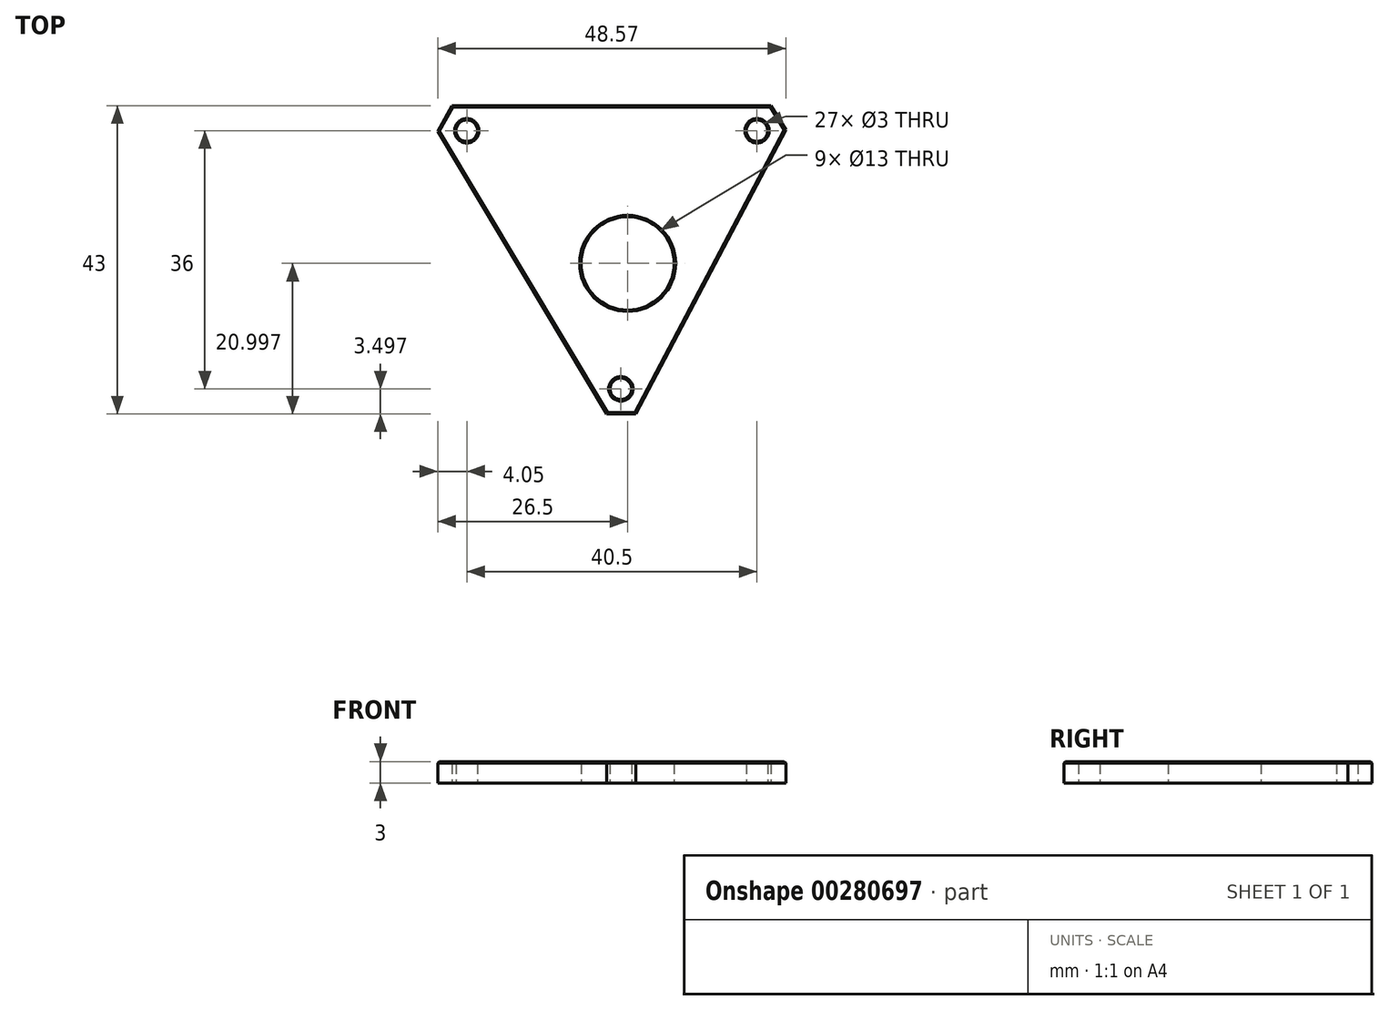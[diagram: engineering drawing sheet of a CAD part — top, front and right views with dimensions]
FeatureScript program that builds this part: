
annotation { "Feature Type Name" : "Feature", "Feature Type Description" : "" }
export const myFeature = defineFeature(function(context is Context, id is Id, definition is map)
    precondition{}
    {
        {
            var Q0;
            Q0=qCreatedBy(makeId("Top.planeOp"),FACE);
            var sketch = newSketch(context, id + "F0", { "sketchPlane" : qUnion([Q0])});
            skCircle(sketch, "E0", {"center": v(-29.37, -2.35) * mm, "radius": 1.5 * mm});
            skLineSegment(sketch, "E1", {"start": v(-29.37, -2.35) * mm, "end": v(-27.87, -2.35) * mm, "construction": true});
            skCircle(sketch, "E2", {"center": v(11.13, -2.35) * mm, "radius": 1.5 * mm});
            skCircle(sketch, "E3", {"center": v(-7.87, -38.35) * mm, "radius": 1.5 * mm});
            skLineSegment(sketch, "E4", {"start": v(-29.37, -2.35) * mm, "end": v(11.13, -2.35) * mm, "construction": true});
            skLineSegment(sketch, "E5", {"start": v(-7.87, -38.35) * mm, "end": v(-7.87, -2.35) * mm, "construction": true});
            skLineSegment(sketch, "E6.bottom", {"start": v(-32.87, 1.15) * mm, "end": v(14.63, 1.15) * mm, "construction": true});
            skLineSegment(sketch, "E6.top", {"start": v(-32.87, -41.85) * mm, "end": v(14.63, -41.85) * mm, "construction": true});
            skLineSegment(sketch, "E6.left", {"start": v(-32.87, 1.15) * mm, "end": v(-32.87, -41.85) * mm, "construction": true});
            skLineSegment(sketch, "E6.right", {"start": v(14.63, 1.15) * mm, "end": v(14.63, -41.85) * mm, "construction": true});
            skLineSegment(sketch, "E7", {"start": v(-29.37, -2.35) * mm, "end": v(-32.87, -2.35) * mm, "construction": true});
            skLineSegment(sketch, "E8", {"start": v(-29.37, -2.35) * mm, "end": v(-29.37, 1.15) * mm, "construction": true});
            skLineSegment(sketch, "E9", {"start": v(11.13, -2.35) * mm, "end": v(14.63, -2.35) * mm, "construction": true});
            skLineSegment(sketch, "E10", {"start": v(-7.87, -38.35) * mm, "end": v(-7.73, -41.85) * mm, "construction": true});
            skCircle(sketch, "E11", {"center": v(-29.37, -2.35) * mm, "radius": 3.5 * mm, "construction": true});
            skCircle(sketch, "E12", {"center": v(11.13, -2.35) * mm, "radius": 3.5 * mm, "construction": true});
            skCircle(sketch, "E13", {"center": v(-7.87, -38.35) * mm, "radius": 3.5 * mm, "construction": true});
            skLineSegment(sketch, "E14", {"start": v(15.15, -2.24) * mm, "end": v(13.1, 1.15) * mm});
            skLineSegment(sketch, "E15", {"start": v(-33.42, -2.4) * mm, "end": v(-31.4, 1.15) * mm});
            skLineSegment(sketch, "E16", {"start": v(-9.86, -41.85) * mm, "end": v(-5.76, -41.85) * mm});
            skLineSegment(sketch, "E17", {"start": v(-9.86, -41.85) * mm, "end": v(-33.42, -2.4) * mm});
            skLineSegment(sketch, "E18", {"start": v(-5.76, -41.85) * mm, "end": v(15.15, -2.24) * mm});
            skLineSegment(sketch, "E19", {"start": v(13.1, 1.15) * mm, "end": v(-31.4, 1.15) * mm});
            skLineSegment(sketch, "E20", {"start": v(-32.41, -0.63) * mm, "end": v(-8.5, -14.2) * mm, "construction": true});
            skLineSegment(sketch, "E21", {"start": v(14.13, -0.55) * mm, "end": v(-8.5, -14.2) * mm, "construction": true});
            skCircle(sketch, "E22", {"center": v(-6.92, -20.85) * mm, "radius": 6.5 * mm});
            skLineSegment(sketch, "E23", {"start": v(-29.37, -2.35) * mm, "end": v(-29.37, -31.87) * mm, "construction": true});
            skSolve(sketch);
        }
        {
            var Q0;
            Q0 = qSketchRegion(id + "F0", true);
            extrude(context, id + "F1", {"entities" : qUnion([Q0]), "depth" : 3 * mm});
        }
        {
            var Q0;
            Q0=makeQuery(id+"F1.opExtrude","CAP_FACE",FACE,{"disambiguationData":[OSD([sQuery(id+"F0.wireOp",EDGE,"E0"),sQuery(id+"F0.wireOp",EDGE,"E2"),sQuery(id+"F0.wireOp",EDGE,"E3"),sQuery(id+"F0.wireOp",EDGE,"E14"),sQuery(id+"F0.wireOp",EDGE,"E15"),sQuery(id+"F0.wireOp",EDGE,"E16"),sQuery(id+"F0.wireOp",EDGE,"E17"),sQuery(id+"F0.wireOp",EDGE,"E18"),sQuery(id+"F0.wireOp",EDGE,"E19"),sQuery(id+"F0.wireOp",EDGE,"E22")])],"isStart":false});
            chamfer(context, id + "F2", {"entities" : qUnion([Q0]), "width" : 0.2 * mm, "tangentPropagation" : true});
        }
    });
